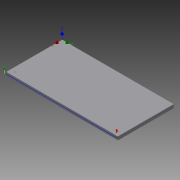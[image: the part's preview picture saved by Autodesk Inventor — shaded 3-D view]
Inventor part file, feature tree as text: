
AUTODESK INVENTOR PART (.ipt)
format: ipt  version: 2015 SP1 (Build 190203100, 203)  size: 153,088 bytes
history: native  units: mm
features: extrude x1, hole x1, pattern_linear x1, sketch x1
ambient origin geometry x8: Origin, YZ Plane, XZ Plane, XY Plane, X Axis, Y Axis, Z Axis, Center Point
bodies: Solid1 (feature_tree)
feature tree (4):
  extrude  "Extrusion1"  Depth=195.0mm
  hole  "Hole1"  [1 undecoded]
  pattern_linear  "Rectangular Pattern1"  Spacing1=15.0mm  [1 undecoded]
  sketch  "Sketch1"  dims[d0=390.0mm d1=195.0mm d2=12.0mm d3=0.0mm d4=15.0mm d5=15.0mm d6=3.0mm d7=6.0mm d8=4.0mm d9=2.0mm d10=90.0deg d11=8.0mm d12=20.594885mm d13=20.0mm d15=200.0mm d16=20.0mm d18=360.0mm]
note: 2 required parameter values undecoded (feature->parameter linkage not recoverable at this tier; creation-order binding heuristic only, values carry confidence <= 0.55)
